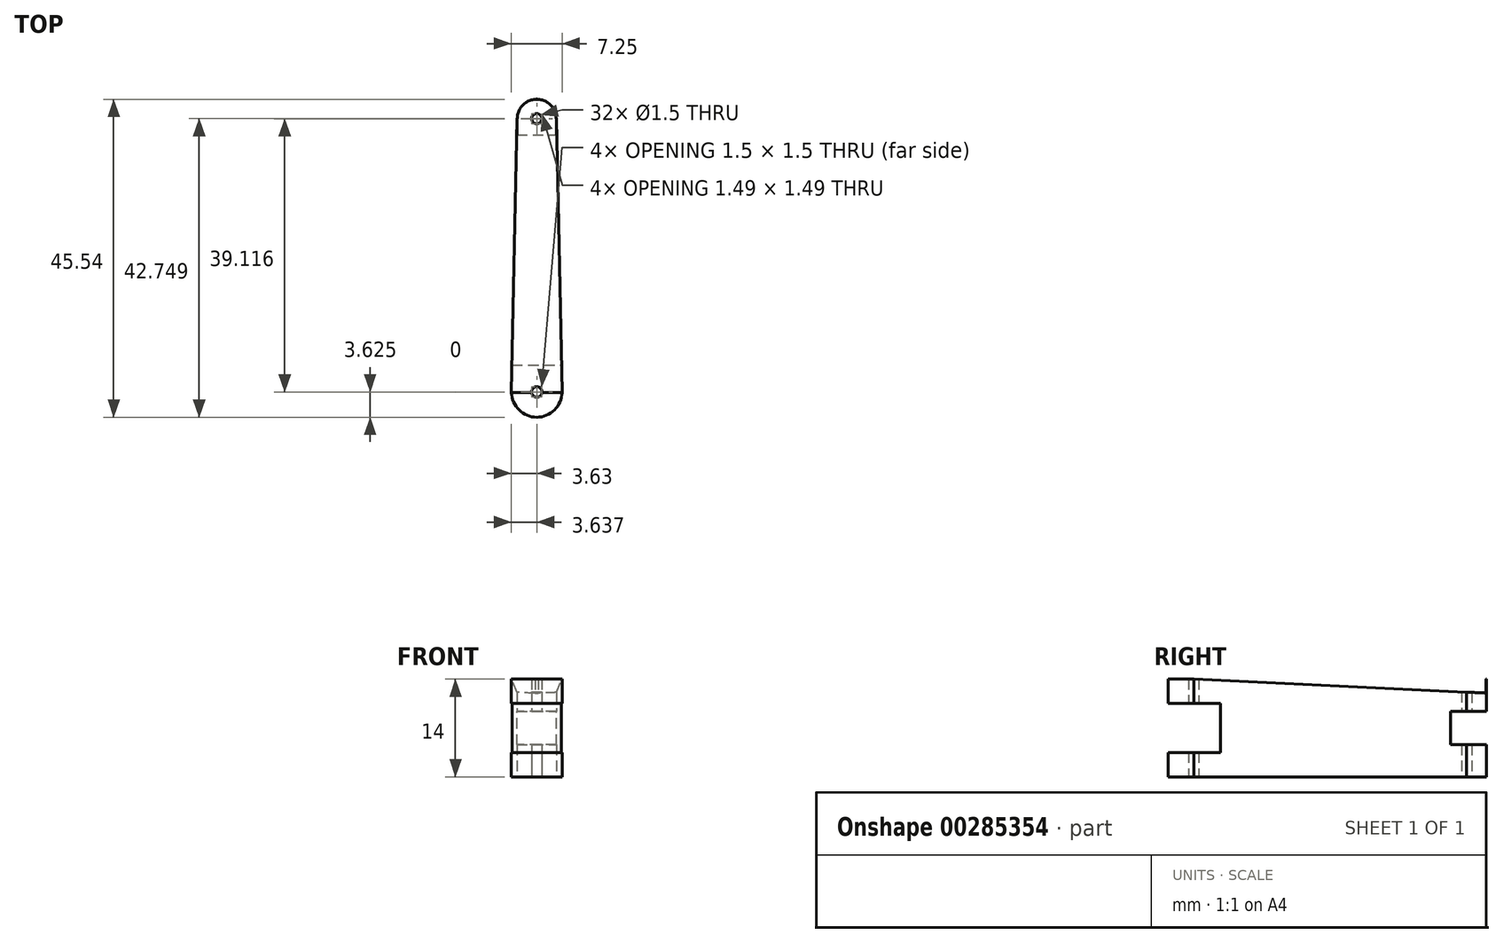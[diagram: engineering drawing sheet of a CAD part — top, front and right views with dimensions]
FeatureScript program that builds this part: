
annotation { "Feature Type Name" : "Feature", "Feature Type Description" : "" }
export const myFeature = defineFeature(function(context is Context, id is Id, definition is map)
    precondition{}
    {
        {
            var Q0;
            Q0=qCreatedBy(makeId("Top.planeOp"),FACE);
            var sketch = newSketch(context, id + "F0", { "sketchPlane" : qUnion([Q0])});
            skCircle(sketch, "E0", {"center": v(0, 13.84) * mm, "radius": 2.8 * mm});
            skCircle(sketch, "E1", {"center": v(0, -25.27) * mm, "radius": 3.62 * mm});
            skLineSegment(sketch, "E2", {"start": v(2.8, 13.84) * mm, "end": v(3.63, -25.27) * mm});
            skLineSegment(sketch, "E3", {"start": v(-2.8, 13.84) * mm, "end": v(-3.63, -25.27) * mm});
            skLineSegment(sketch, "E4", {"start": v(-2.8, 13.84) * mm, "end": v(2.8, 13.84) * mm});
            skLineSegment(sketch, "E5", {"start": v(-3.63, -25.27) * mm, "end": v(3.63, -25.27) * mm});
            skCircle(sketch, "E6", {"center": v(0, -25.27) * mm, "radius": 0.75 * mm});
            skCircle(sketch, "E7", {"center": v(0, 13.84) * mm, "radius": 0.75 * mm});
            skSolve(sketch);
        }
        {
            var Q0;
            {var subQ0=sQuery(id+"F0.wireOp",EDGE,"E2");var subQ1=sQuery(id+"F0.wireOp",EDGE,"E1");var subQ2=makeQuery(id+"F0.imprint","INTERSECT",VERTEX,{"disambiguationData":[OD(1.0)],"derivedFrom":[subQ1,subQ0]});Q0=makeQuery(id+"F0.imprint","IMPRINT",FACE,{"disambiguationData":[TD([[makeQuery(id+"F0.imprint","IMPRINT",EDGE,{"disambiguationData":[TD([[subQ2,-1.0]])],"derivedFrom":subQ1}),1.0]])]});}
            var Q1;
            {var subQ0=sQuery(id+"F0.wireOp",EDGE,"E2");var subQ1=sQuery(id+"F0.wireOp",EDGE,"E0");var subQ2=makeQuery(id+"F0.imprint","INTERSECT",VERTEX,{"derivedFrom":[subQ1,subQ0]});Q1=makeQuery(id+"F0.imprint","IMPRINT",FACE,{"disambiguationData":[TD([[makeQuery(id+"F0.imprint","IMPRINT",EDGE,{"disambiguationData":[TD([[subQ2,1.0]])],"derivedFrom":subQ1}),-1.0]])]});}
            var Q2;
            {var subQ0=sQuery(id+"F0.wireOp",EDGE,"E0");var subQ1=makeQuery(id+"F0.imprint","INTERSECT",VERTEX,{"derivedFrom":[subQ0,sQuery(id+"F0.wireOp",EDGE,"E2")]});Q2=makeQuery(id+"F0.imprint","IMPRINT",FACE,{"disambiguationData":[TD([[makeQuery(id+"F0.imprint","IMPRINT",EDGE,{"disambiguationData":[TD([[subQ1,-1.0]])],"derivedFrom":subQ0}),1.0]])]});}
            var Q3;
            {var subQ0=sQuery(id+"F0.wireOp",EDGE,"E5");Q3=makeQuery(id+"F0.imprint","IMPRINT",FACE,{"disambiguationData":[TD([[makeQuery(id+"F0.imprint","IMPRINT",EDGE,{"derivedFrom":subQ0}),-1.0]])]});}
            var Q4;
            {var subQ0=sQuery(id+"F0.wireOp",EDGE,"E4");Q4=makeQuery(id+"F0.imprint","IMPRINT",FACE,{"disambiguationData":[TD([[makeQuery(id+"F0.imprint","IMPRINT",EDGE,{"derivedFrom":subQ0}),-1.0]])]});}
            extrude(context, id + "F1", {"entities" : qUnion([Q0, Q1, Q2, Q3, Q4]), "depth" : 14 * mm});
        }
        {
            var Q0;
            Q0=qCreatedBy(makeId("Right.planeOp"),FACE);
            var sketch = newSketch(context, id + "F2", { "sketchPlane" : qUnion([Q0])});
            skLineSegment(sketch, "E8.bottom", {"start": v(-50.52, 0) * mm, "end": v(33.89, 0) * mm});
            skLineSegment(sketch, "E8.top", {"start": v(-50.52, 7) * mm, "end": v(33.89, 7) * mm});
            skLineSegment(sketch, "E8.left", {"start": v(-50.52, 0) * mm, "end": v(-50.52, 7) * mm});
            skLineSegment(sketch, "E8.right", {"start": v(33.89, 0) * mm, "end": v(33.89, 7) * mm});
            skPoint(sketch, "E9.middle", {"position": v(17.27, 7) * mm});
            skLineSegment(sketch, "E10", {"start": v(-28.9, 0) * mm, "end": v(16.63, 2) * mm});
            skLineSegment(sketch, "E11", {"start": v(16.63, 12) * mm, "end": v(-28.9, 14.17) * mm});
            skLineSegment(sketch, "E12", {"start": v(-28.9, 14.17) * mm, "end": v(-28.9, 0) * mm});
            skLineSegment(sketch, "E13", {"start": v(16.63, 12) * mm, "end": v(16.63, 18.46) * mm});
            skLineSegment(sketch, "E14", {"start": v(16.63, 18.46) * mm, "end": v(-28.9, 17.28) * mm});
            skLineSegment(sketch, "E15", {"start": v(-28.9, 17.28) * mm, "end": v(-28.9, 14.17) * mm});
            skLineSegment(sketch, "E16", {"start": v(16.63, 2) * mm, "end": v(16.84, -2.7) * mm});
            skLineSegment(sketch, "E17", {"start": v(16.84, -2.7) * mm, "end": v(-28.9, -2.7) * mm});
            skLineSegment(sketch, "E18", {"start": v(-28.9, -2.7) * mm, "end": v(-28.9, 0) * mm});
            skLineSegment(sketch, "E19", {"start": v(16.63, 2) * mm, "end": v(-28.9, 0) * mm});
            skLineSegment(sketch, "E20", {"start": v(-28.9, 0) * mm, "end": v(-28.9, -2.7) * mm});
            skLineSegment(sketch, "E21", {"start": v(16.84, -2.7) * mm, "end": v(16.63, 2) * mm});
            skLineSegment(sketch, "E22.bottom", {"start": v(23.02, 4.6) * mm, "end": v(11.52, 4.6) * mm});
            skLineSegment(sketch, "E22.top", {"start": v(23.02, 9.4) * mm, "end": v(11.52, 9.4) * mm});
            skLineSegment(sketch, "E22.left", {"start": v(23.02, 4.6) * mm, "end": v(23.02, 9.4) * mm});
            skLineSegment(sketch, "E22.right", {"start": v(11.52, 4.6) * mm, "end": v(11.52, 9.4) * mm});
            skLineSegment(sketch, "E23.bottom", {"start": v(-29.04, 3.5) * mm, "end": v(-21.44, 3.5) * mm});
            skLineSegment(sketch, "E23.top", {"start": v(-29.04, 10.5) * mm, "end": v(-21.44, 10.5) * mm});
            skLineSegment(sketch, "E23.left", {"start": v(-29.04, 3.5) * mm, "end": v(-29.04, 10.5) * mm});
            skLineSegment(sketch, "E23.right", {"start": v(-21.44, 3.5) * mm, "end": v(-21.44, 10.5) * mm});
            skPoint(sketch, "E23.middle", {"position": v(-25.24, 7) * mm});
            skSolve(sketch);
        }
        {
            var Q0;
            Q0=makeQuery(id+"F2.imprint","IMPRINT",FACE,{"disambiguationData":[TD([[makeQuery(id+"F2.imprint","IMPRINT",EDGE,{"derivedFrom":sQuery(id+"F2.wireOp",EDGE,"E11")}),-1.0]])]});
            var Q1;
            {var subQ0=sQuery(id+"F2.wireOp",EDGE,"E19");Q1=makeQuery(id+"F2.imprint","IMPRINT",FACE,{"disambiguationData":[TD([[makeQuery(id+"F2.imprint","IMPRINT",EDGE,{"derivedFrom":subQ0}),1.0]])]});}
            var Q2;
            {var subQ5=sQuery(id+"F2.wireOp",EDGE,"E22.bottom");Q2=makeQuery(id+"F2.imprint","IMPRINT",FACE,{"disambiguationData":[TD([[makeQuery(id+"F2.imprint","IMPRINT",EDGE,{"derivedFrom":subQ5}),-1.0]])]});}
            var Q3;
            {var subQ5=sQuery(id+"F2.wireOp",EDGE,"E22.top");Q3=makeQuery(id+"F2.imprint","IMPRINT",FACE,{"disambiguationData":[TD([[makeQuery(id+"F2.imprint","IMPRINT",EDGE,{"derivedFrom":subQ5}),1.0]])]});}
            var Q4;
            {var subQ0=sQuery(id+"F2.wireOp",EDGE,"E23.right");var subQ1=sQuery(id+"F2.wireOp",EDGE,"E8.top");var subQ2=makeQuery(id+"F2.imprint","INTERSECT",VERTEX,{"derivedFrom":[subQ1,subQ0]});Q4=makeQuery(id+"F2.imprint","IMPRINT",FACE,{"disambiguationData":[TD([[makeQuery(id+"F2.imprint","IMPRINT",EDGE,{"disambiguationData":[TD([[subQ2,1.0]])],"derivedFrom":subQ1}),1.0]])]});}
            var Q5;
            {var subQ0=sQuery(id+"F2.wireOp",EDGE,"E23.right");var subQ1=sQuery(id+"F2.wireOp",EDGE,"E8.top");var subQ2=makeQuery(id+"F2.imprint","INTERSECT",VERTEX,{"derivedFrom":[subQ1,subQ0]});Q5=makeQuery(id+"F2.imprint","IMPRINT",FACE,{"disambiguationData":[TD([[makeQuery(id+"F2.imprint","IMPRINT",EDGE,{"disambiguationData":[TD([[subQ2,1.0]])],"derivedFrom":subQ1}),-1.0]])]});}
            extrude(context, id + "F3", {"entities" : qUnion([Q0, Q1, Q2, Q3, Q4, Q5]), "operationType" : NewBodyOperationType.REMOVE, "endBound" : BoundingType.SYMMETRIC, "oppositeDirection" : true, "depth" : 25 * mm});
        }
    });
